# Revit family: JAVA_20W_3000K_1675LM
name_source: partatom
category: Lighting Fixtures
units: mm (PartAtom-declared; Revit-internal decimal feet)

## family parameters
Always vertical = Yes
Cut with Voids When Loaded = No
Host = Wall
Light Source = Yes
OmniClass Number = 23.80.70.00
OmniClass Title = Lighting
Part Type = Normal
Room Calculation Point = No
Round Connector Dimension = Use Diameter
Shared = No

## types (1)
- JAVA_20W_3000K_1675LM
    Color Filter = 16777215
    Default Elevation = 0 mm  [stored 0 ft]
    Dimensions = 600 x 65 x 53 mm
    Dimming Lamp Color Temperature Shift = <None>
    Emit from Line Length = 610 mm
    Fintion = Chrome
    IRC = >80
    Matériau = Corps en aluminium
    Photometric Web File = google_eulumdat_converter (29).ies
    Puissance nominale = 20W
    Tension = AC 220-240V
    Tilt Angle = 90.00°
    Type = Applique salle de bain
    Type de lampe = LED

note: [stored X ft] marks values corroborated as IEEE doubles in the binary element streams (Revit-internal decimal feet)

## geometry (parser evidence)
native form markers: Sweep x1
no freeform markers — native parametric forms only
